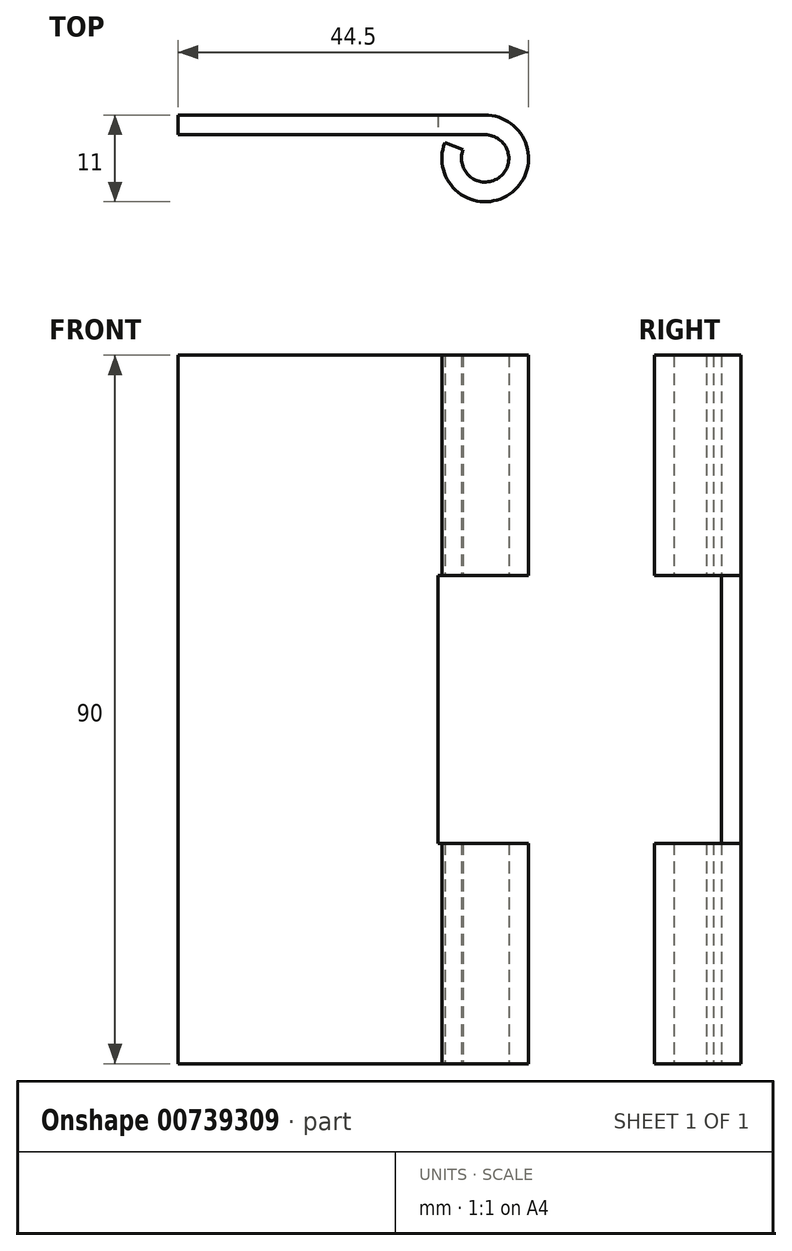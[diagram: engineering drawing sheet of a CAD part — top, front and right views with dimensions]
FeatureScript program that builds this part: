
annotation { "Feature Type Name" : "Feature", "Feature Type Description" : "" }
export const myFeature = defineFeature(function(context is Context, id is Id, definition is map)
    precondition{}
    {
        {
            var Q0;
            Q0=qCreatedBy(makeId("Top.planeOp"),FACE);
            var sketch = newSketch(context, id + "F0", { "sketchPlane" : qUnion([Q0])});
            skArc(sketch, "E0", {"start": v(-5.12, 2) * mm, "mid": v(3.1, -4.54) * mm, "end": v(0, 5.5) * mm});
            skLineSegment(sketch, "E1", {"start": v(0, 5.5) * mm, "end": v(-39, 5.5) * mm});
            skLineSegment(sketch, "E2.0", {"start": v(0, 3) * mm, "end": v(-39, 3) * mm});
            skArc(sketch, "E2.1", {"start": v(-2.8, 1.1) * mm, "mid": v(1.7, -2.48) * mm, "end": v(0, 3) * mm});
            skLineSegment(sketch, "E3", {"start": v(-39, 5.5) * mm, "end": v(-39, 3) * mm});
            skLineSegment(sketch, "E4", {"start": v(-2.8, 1.1) * mm, "end": v(-5.12, 2) * mm});
            skSolve(sketch);
        }
        {
            var Q0;
            Q0=makeQuery(id+"F0.imprint","IMPRINT",FACE,{"disambiguationData":[TD([[makeQuery(id+"F0.imprint","IMPRINT",EDGE,{"derivedFrom":sQuery(id+"F0.wireOp",EDGE,"E0")}),1.0]])]});
            extrude(context, id + "F1", {"entities" : qUnion([Q0]), "endBound" : BoundingType.SYMMETRIC, "depth" : 90 * mm, "offsetDistance" : 25 * mm});
        }
        {
            var Q0;
            Q0=qCreatedBy(makeId("Top.planeOp"),FACE);
            var sketch = newSketch(context, id + "F2", { "sketchPlane" : qUnion([Q0])});
            skLineSegment(sketch, "E5.bottom", {"start": v(9, 10) * mm, "end": v(-6, 10) * mm});
            skLineSegment(sketch, "E5.top", {"start": v(9, -10) * mm, "end": v(-6, -10) * mm});
            skLineSegment(sketch, "E5.left", {"start": v(9, 10) * mm, "end": v(9, -10) * mm});
            skLineSegment(sketch, "E5.right", {"start": v(-6, 10) * mm, "end": v(-6, -10) * mm});
            skPoint(sketch, "E5.middle", {"position": v(1.5, 0) * mm});
            skSolve(sketch);
        }
        {
            var Q0;
            Q0=makeQuery(id+"F2.imprint","IMPRINT",FACE,{"disambiguationData":[TD([[makeQuery(id+"F2.imprint","IMPRINT",EDGE,{"derivedFrom":sQuery(id+"F2.wireOp",EDGE,"E5.bottom")}),1.0]])]});
            extrude(context, id + "F3", {"entities" : qUnion([Q0]), "operationType" : NewBodyOperationType.REMOVE, "endBound" : BoundingType.SYMMETRIC, "depth" : 34 * mm, "offsetDistance" : 25 * mm});
        }
    });
